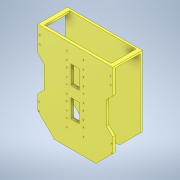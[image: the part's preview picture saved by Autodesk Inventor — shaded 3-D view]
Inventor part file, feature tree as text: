
AUTODESK INVENTOR PART (.ipt)
format: ipt  version: 2021 (Build 250183000, 183)  size: 318,976 bytes
history: native  units: mm
features: extrude x11, sketch x11, other x1, chamfer x1
ambient origin geometry x8: Origin, YZ Plane, XZ Plane, XY Plane, X Axis, Y Axis, Z Axis, Center Point
bodies: Body1 (feature_tree), Body2 (feature_tree)
feature tree (24):
  other  "Sólido1"
  extrude  "Extrusión1"  Depth=120.0mm
  extrude  "Extrusión2"  Depth=180.0mm
  extrude  "Extrusión3"  Depth=100.0mm
  extrude  "Extrusión4"  Depth=12.55mm TaperAngle=0.0deg
  extrude  "Extrusión6"  Depth=30.0mm
  extrude  "Extrusión7"  Depth=30.0mm
  extrude  "Extrusión8"  Depth=10.0mm
  extrude  "Extrusión9"  Depth=5.0mm
  extrude  "Extrusión10"  Depth=19.5mm
  extrude  "Extrusión11"  Depth=40.0mm
  chamfer  "Chaflán1"  Distance=19.5mm
  extrude  "Extrusión12"  Depth=125.0mm
  sketch  "Boceto1"  dims[d0=120.0mm d1=70.0mm]
  sketch  "Boceto2"  dims[d2=110.0mm d3=180.0mm]
  sketch  "Boceto3"  dims[d8=100.0mm d9=80.0mm]
  sketch  "Boceto4"  dims[d13=150.0mm d14=12.55mm d15=0.0mm]
  sketch  "Boceto6"  dims[d17=80.0mm d18=30.0mm]
  sketch  "Boceto7"  dims[d19=30.0mm d20=60.0mm]
  sketch  "Boceto8"  dims[d22=30.0mm d23=10.0mm]
  sketch  "Boceto9"  dims[d25=39.0mm d26=5.0mm]
  sketch  "Boceto10"  dims[d27=14.75mm d28=0.0mm d29=19.5mm]
  sketch  "Boceto11"  dims[d30=70.0mm d31=40.0mm]
  sketch  "Boceto12"  dims[d32=80.0mm d33=19.5mm d34=5.0mm d35=14.75mm d36=0.0mm d37=70.0mm d38=70.0mm d39=35.0mm d40=5.0mm d41=39.0mm d42=5.0mm d43=5.0mm d44=14.75mm d45=0.0mm d46=70.0mm d56=40.0mm d57=25.0mm d58=25.0mm d59=14.75mm d60=0.0mm d63=25.0mm d64=40.0mm d65=25.0mm d66=40.0mm d67=14.75mm d68=0.0mm d69=20.0mm d70=45.0mm d71=90.0mm d72=10.0mm d73=10.0mm d74=10.0mm d75=10.0mm d76=10.0mm d77=10.0mm d78=85.0mm d79=10.0mm d80=10.0mm d81=10.0mm d82=85.0mm d83=10.0mm d84=10.0mm d85=10.0mm d86=7.0mm d87=0.0mm d88=10.0mm d89=20.0mm d90=10.0mm d91=20.0mm d92=130.0mm d93=0.0mm d94=10.0mm d95=10.0mm d96=320.0mm d97=0.0mm d98=430.0mm d99=0.0mm d100=100.0mm d101=2.0mm d102=45.0deg d103=20.0mm d104=40.0mm d105=15.0mm d106=40.0mm d107=125.0mm d108=0.0mm]
